# Revit family: BE_84514_de_DE_Scheinwerfer
name_source: partatom
category: Leuchten
revit_build: Autodesk Revit 2015 (Build: 20160512_0715(x64)
units: mm (PartAtom-declared; Revit-internal decimal feet)

## types (1)
- BEGA_84514_Grafit
    AC/DC = AC/DC
    Aktualisierung = 2017-08-01T04:09:12
    BEGA_Dummy = Nein
    BEGA_IES1 = Ja
    BEGA_IES2 = Ja
    BEGA_IES3 = Ja
    BEGA_Intern = Ja
    BEGA_Intern_Konstruktion = Ja
    BEGA_Intern_an = Ja
    BEGA_Intern_aus = Ja
    Beschreibung = Hochleistungsscheinwerfer RGBW
    Beschreibung_Sonderanfertigung = Hier können Sie Informationen zur Sonderanfertigung eintragen.
    Bestellnummer = 84514
    CE_Konformität = ja
    Energieeffizienzklasse = LED A++ - A
    Frequenz = 0/50-60 Hz
    Gewicht = 24.9 kg
    Hersteller = BEGA
    LED_Modulbezeichnung = 4x LED-0801/RGBW
    Lampe = LED 326.8 W
    Lastklassifizierung = Beleuchtung
    Lebensdauerkriterien = L70B50 @ 25 °C =  h
    Leuchtenlichtstrom = 20595 lm
    Logo = BEGA_Logo.png
    M_A = Nein
    M_G = Ja
    M_W = Nein
    Material_02 = BEGA_Oberfläche_Silber_matt
    Material_03 = BEGA_Oberfläche_Weiss_matt
    Material_06 = BEGA_Oberfläche_Edelstahl_gebürstet
    Material_09 = BEGA_Glas_klar
    Material_11 = BEGA_Glas_opal
    Material_15 = BEGA_Leuchtmedium_matt
    Material_17 = BEGA_Reflektor
    Material_18 = BEGA_Gummi_schwarz
    Modell = 84514
    Produktdatenblatt = http://www.bega.de
    Scheinlast = 0 VA
    Schutzart = IP 67
    Schutzklasse = I
    Sonderanfertigung = Nein
    Spannung = 240 V
    Typenbild = 84514.png
    URL = http://www.bega.de
    Umgebungstemperatur = 25 °C
    Vorgabe-Ansicht = 0 mm  [stored 0 ft]
    Windangriffsfläche = 0.38 m²

note: [stored X ft] marks values corroborated as IEEE doubles in the binary element streams (Revit-internal decimal feet)

## geometry (parser evidence)
native form markers: Blend x4, Sweep x13
no freeform markers — native parametric forms only
